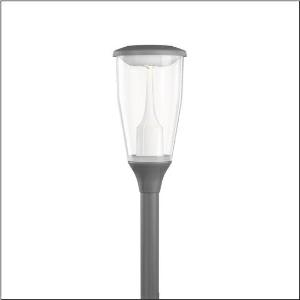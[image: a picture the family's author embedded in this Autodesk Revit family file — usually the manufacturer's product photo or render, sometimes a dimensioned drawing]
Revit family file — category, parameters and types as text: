
# Revit family: dl_11_iq___st1_2a_5xa5575af14h000022_aeb9
name_source: partatom
category: Lighting Fixtures
units: mm (PartAtom-declared; Revit-internal decimal feet)

## family parameters
Cut with Voids When Loaded = No
Host = Face
Light Source = No
Part Type = Normal
Room Calculation Point = No
Round Connector Dimension = Use Diameter
Shared = No

## types (1)
- --- (1 x LED, 1560 lm, 12.9 W, 2200K)
    Apparent Load = 13 VA
    CIE Flux Codes = 24 63 94 96 100
    Color Rendering = 70
    Color Temperature = 2200K
    Default Elevation = 1800 mm
    Description = DL 11 iQ, mast luminaire, Module 540 iQ-SR, primary light control with 3 zone facetted reflector, of plastic, silver coated, highly specular, structured, primary optical cover: cover, of PMMA, transparent, light distribution: ST1.2a, light emission: direct distribution, primary light characteristic: asymmetric, installation type: post-top, LED, High Power LED, rated luminous flux: 1.560lm, luminous efficacy: 149lm/W, light colour: 722, colour temperature: 2200K, control: Street-Remote, Auto-Match, Temp-Guard, Lumen-Switch, Night-Set, Smart-Wire, Light-Fading, Desk-Remote (wireless, voltage-free reading and setting of iQ features in the workshop via application-optimized NFC function/RFID function), optimised constant luminous flux control (CLO 2.0), mains connection: 220..240V, AC, 50/60Hz, connection cable pre-assembled, cable length: 5,5m, wiring characteristics: H07RN-F, 5-core, 1.5mm², start of lifetime: 13W, end of service life: 13W, reduction: 5W, luminaire housing, upper part, of diecast aluminium, coated, Siteco® metallic grey (DB 702S), spigot size: 76mm (post-top), post-top mast mounting element, of diecast aluminium, coated, Siteco® metallic grey (DB 702S), Module 540 iQ-SR, traffic white (RAL 9016), equipment: standard, protection rating (complete): IP66, insulation class (complete): insulation class II (safety insulation), certification: CE, ENEC, ENEC+, VDE, packaging unit: 1 piece

Light Distribution: ST1.2a
    Height = 665 mm
    Lamp = 1 x LED
    Lamp Light Flux = 1560 lm
    Lamp Power = 12.9 W
    Lamp count = 1
    Length = 334 mm
    Luminous efficacy = 121 lm/W
    Manufacturer = Siteco
    ModVariant = No
    Model = 5XA5575AF14H000022
    Number of Poles = 1
    OnlyDefault = Yes
    Power Factor = 1
    Product Name = DL 11 iQ | ST1.2a
    Product group = mast luminaire | pylon top
    ProductGroupID = 6100
    Protection Class = Protection class II
    Protection Degree = IP 66
    RLX_Detail_Level = 1
    RLX_Emergency_Light_Flux = 0 lm
    RLX_Emergency_Type = 0
    RLX_Emergency_Type_DB = No
    RlxData = <blob elided: 153981 chars, md5=0cc702dd>
    Socket = socket
    Standby Power = 0 W
    System Light Flux = 1560 lm
    System Power = 13 W
    Type Comments = factory setting: luminous flux: 100 % | dim-lin: 254 | 516 mA
    Type Image = l_1258354.jpg
    URL = http://relux.com
    VarID = @adj_043963
    Voltage = 0 V
    Weight = 0.00 kg
    Width = 0 mm  [stored 0 ft]

note: [stored X ft] marks values corroborated as IEEE doubles in the binary element streams (Revit-internal decimal feet)

## geometry (parser evidence)
native form markers: Blend x4, Sweep x10
no freeform markers — native parametric forms only
